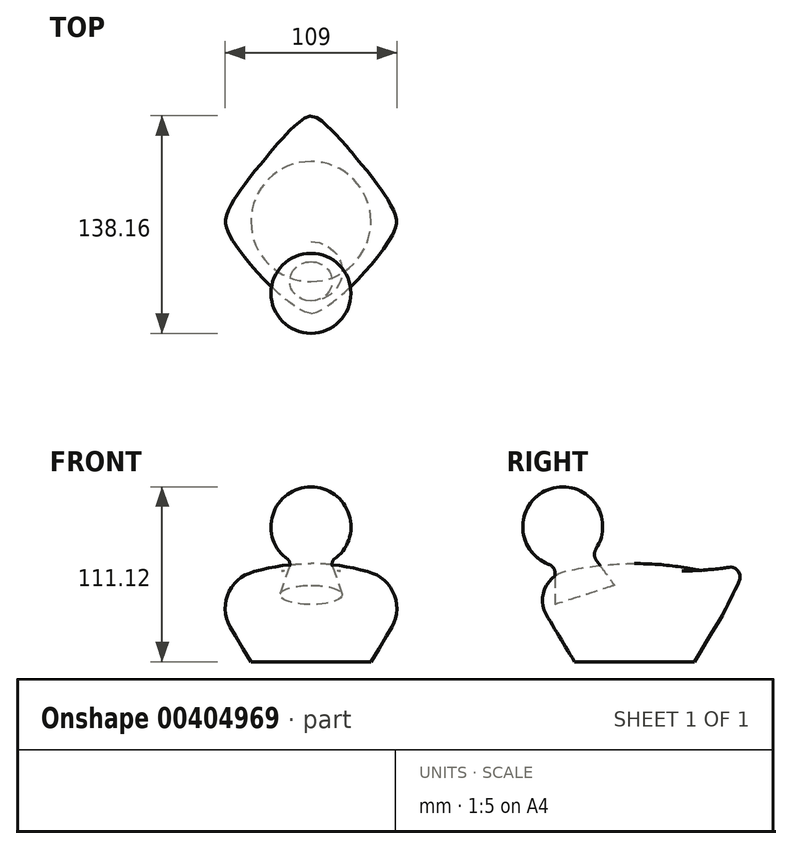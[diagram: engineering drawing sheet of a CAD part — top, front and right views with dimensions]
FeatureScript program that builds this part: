
annotation { "Feature Type Name" : "Feature", "Feature Type Description" : "" }
export const myFeature = defineFeature(function(context is Context, id is Id, definition is map)
    precondition{}
    {
        {
            var Q0;
            Q0=qCreatedBy(makeId("Top.planeOp"),FACE);
            var sketch = newSketch(context, id + "F0", { "sketchPlane" : qUnion([Q0])});
            skCircle(sketch, "E0", {"center": v(0, 0) * mm, "radius": 38.1 * mm});
            skSolve(sketch);
        }
        {
            var Q0;
            Q0=qCreatedBy(makeId("Right.planeOp"),FACE);
            var sketch = newSketch(context, id + "F1", { "sketchPlane" : qUnion([Q0])});
            skLineSegment(sketch, "E1.0", {"start": v(-38.1, 0) * mm, "end": v(38.1, 0) * mm, "construction": true});
            skLineSegment(sketch, "E2", {"start": v(-38.1, 0) * mm, "end": v(-55.66, 29.2) * mm});
            skLineSegment(sketch, "E3", {"start": v(38.1, 0) * mm, "end": v(55.66, 29.2) * mm});
            skLineSegment(sketch, "E4", {"start": v(-55.66, 29.2) * mm, "end": v(55.66, 29.2) * mm, "construction": true});
            skPoint(sketch, "E5.center.orphan", {"position": v(0, 29.2) * mm});
            skPoint(sketch, "E6.center.orphan", {"position": v(0, 968.99) * mm});
            skArc(sketch, "E7", {"start": v(43.4, 57.64) * mm, "mid": v(0, 62.33) * mm, "end": v(-43.4, 57.64) * mm});
            skArc(sketch, "E8", {"start": v(-43.4, 57.64) * mm, "mid": v(-56.83, 46.57) * mm, "end": v(-55.66, 29.2) * mm});
            skArc(sketch, "E9", {"start": v(55.66, 29.2) * mm, "mid": v(56.83, 46.57) * mm, "end": v(43.4, 57.64) * mm});
            skLineSegment(sketch, "E10", {"start": v(-39.34, 39.03) * mm, "end": v(39.34, 39.03) * mm, "construction": true});
            skSolve(sketch);
        }
        {
            var Q0;
            Q0=qCreatedBy(makeId("Front.planeOp"),FACE);
            var sketch = newSketch(context, id + "F2", { "sketchPlane" : qUnion([Q0])});
            skArc(sketch, "E11", {"start": v(37.58, 56.76) * mm, "mid": v(0, 62.33) * mm, "end": v(-37.58, 56.76) * mm});
            skLineSegment(sketch, "E12", {"start": v(-37.58, 56.76) * mm, "end": v(37.58, 56.76) * mm, "construction": true});
            skLineSegment(sketch, "E13", {"start": v(0, 56.76) * mm, "end": v(0, 62.33) * mm, "construction": true});
            skLineSegment(sketch, "E14.0", {"start": v(-38.1, 0) * mm, "end": v(38.1, 0) * mm, "construction": true});
            skLineSegment(sketch, "E15", {"start": v(-38.1, 0) * mm, "end": v(-51.1, 21.7) * mm, "construction": true});
            skPoint(sketch, "E16.start.orphan", {"position": v(-64.12, 43.4) * mm});
            skLineSegment(sketch, "E17", {"start": v(38.1, 0) * mm, "end": v(51.1, 21.7) * mm, "construction": true});
            skArc(sketch, "E18", {"start": v(-37.58, 56.76) * mm, "mid": v(-52.9, 42.53) * mm, "end": v(-51.1, 21.7) * mm});
            skArc(sketch, "E19", {"start": v(51.1, 21.7) * mm, "mid": v(52.9, 42.53) * mm, "end": v(37.58, 56.76) * mm});
            skLineSegment(sketch, "E20", {"start": v(-30.67, 33.95) * mm, "end": v(30.67, 33.95) * mm, "construction": true});
            skLineSegment(sketch, "E21.0", {"start": v(51.1, 21.7) * mm, "end": v(-51.1, 21.7) * mm, "construction": true});
            skSolve(sketch);
        }
        {
            var Q0;
            Q0=qCreatedBy(makeId("Right.planeOp"),FACE);
            var sketch = newSketch(context, id + "F3", { "sketchPlane" : qUnion([Q0])});
            skLineSegment(sketch, "E22.0", {"start": v(-38.1, 0) * mm, "end": v(-55.66, 29.2) * mm});
            skArc(sketch, "E23.0", {"start": v(-43.4, 57.64) * mm, "mid": v(-56.83, 46.57) * mm, "end": v(-55.66, 29.2) * mm});
            skArc(sketch, "E24.0", {"start": v(0, 62.33) * mm, "mid": v(-21.83, 61.15) * mm, "end": v(-43.4, 57.64) * mm});
            skPoint(sketch, "E25", {"position": v(0, 62.33) * mm});
            skPoint(sketch, "E26.orphan", {"position": v(43.4, 57.64) * mm});
            skSolve(sketch);
        }
        {
            var Q0;
            Q0=qCreatedBy(makeId("Front.planeOp"),FACE);
            var sketch = newSketch(context, id + "F4", { "sketchPlane" : qUnion([Q0])});
            skPoint(sketch, "E27.0", {"position": v(38.1, 0) * mm});
            skArc(sketch, "E28.0", {"start": v(51.1, 21.7) * mm, "mid": v(52.9, 42.53) * mm, "end": v(37.58, 56.76) * mm});
            skArc(sketch, "E29.0", {"start": v(37.58, 56.76) * mm, "mid": v(19, 60.93) * mm, "end": v(0, 62.33) * mm});
            skLineSegment(sketch, "E30.0", {"start": v(38.1, 0) * mm, "end": v(51.1, 21.7) * mm});
            skPoint(sketch, "E31.0", {"position": v(0, 62.33) * mm});
            skPoint(sketch, "E32.orphan", {"position": v(-37.58, 56.76) * mm});
            skSolve(sketch);
        }
        {
            var Q0;
            Q0=qCreatedBy(makeId("Right.planeOp"),FACE);
            var sketch = newSketch(context, id + "F5", { "sketchPlane" : qUnion([Q0])});
            skLineSegment(sketch, "E33.0", {"start": v(38.1, 0) * mm, "end": v(55.54, 29) * mm});
            skArc(sketch, "E34.0", {"start": v(42.31, 57.87) * mm, "mid": v(21.27, 61.21) * mm, "end": v(0, 62.33) * mm});
            skPoint(sketch, "E35.0", {"position": v(0, 62.33) * mm});
            skPoint(sketch, "E36.orphan", {"position": v(-43.4, 57.64) * mm});
            skPoint(sketch, "E37.0.end.orphan", {"position": v(43.4, 57.64) * mm});
            skPoint(sketch, "E37.0.start.orphan", {"position": v(55.66, 29.2) * mm});
            skPoint(sketch, "E38", {"position": v(71.96, 61.72) * mm});
            skLineSegment(sketch, "E39", {"start": v(55.77, 29.43) * mm, "end": v(66.52, 50.87) * mm});
            skLineSegment(sketch, "E40", {"start": v(44.53, 57.8) * mm, "end": v(59.94, 60) * mm});
            skArc(sketch, "E41.filletArc", {"start": v(42.31, 57.87) * mm, "mid": v(43.42, 57.74) * mm, "end": v(44.53, 57.8) * mm});
            skArc(sketch, "E42.filletArc", {"start": v(66.52, 50.87) * mm, "mid": v(66, 57.43) * mm, "end": v(59.94, 60) * mm});
            skArc(sketch, "E43.filletArc", {"start": v(55.54, 29) * mm, "mid": v(55.66, 29.21) * mm, "end": v(55.77, 29.43) * mm});
            skSolve(sketch);
        }
        {
            var Q0;
            Q0=qCreatedBy(makeId("Front.planeOp"),FACE);
            var sketch = newSketch(context, id + "F6", { "sketchPlane" : qUnion([Q0])});
            skLineSegment(sketch, "E44.0", {"start": v(-38.1, 0) * mm, "end": v(-51.1, 21.7) * mm});
            skArc(sketch, "E45.0", {"start": v(-37.58, 56.76) * mm, "mid": v(-52.9, 42.53) * mm, "end": v(-51.1, 21.7) * mm});
            skArc(sketch, "E46.0", {"start": v(0, 62.33) * mm, "mid": v(-19, 60.93) * mm, "end": v(-37.58, 56.76) * mm});
            skPoint(sketch, "E47.0", {"position": v(0, 62.33) * mm});
            skPoint(sketch, "E48.orphan", {"position": v(37.58, 56.76) * mm});
            skSolve(sketch);
        }
        {
            var Q0;
            Q0=sQuery(id+"F0.wireOp",EDGE,"E0");
            var Q1;
            Q1=sQuery(id+"F3.wireOp",VERTEX,"E25");
            var Q2;
            Q2 = qBodyType(qCreatedBy(id + "F4" ,EDGE), BodyType.WIRE);
            var Q3;
            Q3 = qBodyType(qCreatedBy(id + "F3" ,EDGE), BodyType.WIRE);
            var Q4;
            Q4 = qBodyType(qCreatedBy(id + "F5" ,EDGE), BodyType.WIRE);
            var Q5;
            Q5 = qBodyType(qCreatedBy(id + "F6" ,EDGE), BodyType.WIRE);
            loft(context, id + "F7", {"bodyType" : ToolBodyType.SURFACE, "addGuides" : true, "wireProfilesArray" : [{ "wireProfileEntities" : qUnion([Q0]) }, { "wireProfileEntities" : qUnion([Q1]) }], "guidesArray" : [{ "guideEntities" : qUnion([Q2]), "guideDerivativeType" : LoftGuideDerivativeType.DEFAULT, "guideDerivativeMagnitude" : 1 }, { "guideEntities" : qUnion([Q3]), "guideDerivativeType" : LoftGuideDerivativeType.DEFAULT, "guideDerivativeMagnitude" : 1 }, { "guideEntities" : qUnion([Q4]), "guideDerivativeType" : LoftGuideDerivativeType.DEFAULT, "guideDerivativeMagnitude" : 1 }, { "guideEntities" : qUnion([Q5]), "guideDerivativeType" : LoftGuideDerivativeType.DEFAULT, "guideDerivativeMagnitude" : 1 }]});
        }
        {
            var Q0;
            Q0=qCreatedBy(makeId("Right.planeOp"),FACE);
            var sketch = newSketch(context, id + "F8", { "sketchPlane" : qUnion([Q0])});
            skArc(sketch, "E49", {"start": v(-53.39, 109.88) * mm, "mid": v(-70.97, 86.32) * mm, "end": v(-54.52, 61.94) * mm});
            skLineSegment(sketch, "E50", {"start": v(-45.57, 85.72) * mm, "end": v(-31.6, 42.47) * mm, "construction": true});
            skLineSegment(sketch, "E51", {"start": v(-31.6, 42.47) * mm, "end": v(-50.4, 36.38) * mm, "construction": true});
            skLineSegment(sketch, "E52", {"start": v(-50.4, 36.38) * mm, "end": v(-50.4, 56) * mm});
            skLineSegment(sketch, "E53", {"start": v(-45.57, 85.72) * mm, "end": v(-53.39, 109.88) * mm, "construction": true});
            skPoint(sketch, "E54.visualSharp", {"position": v(-50.4, 60.78) * mm});
            skArc(sketch, "E54.filletArc", {"start": v(-50.4, 56) * mm, "mid": v(-51.54, 59.62) * mm, "end": v(-54.52, 61.94) * mm});
            skSolve(sketch);
        }
        {
            var Q0;
            Q0=sQuery(id+"F8.wireOp",EDGE,"E49");
            var Q1;
            Q1=sQuery(id+"F8.wireOp",EDGE,"E52");
            var Q2;
            Q2=sQuery(id+"F8.wireOp",EDGE,"E54.filletArc");
            var Q3;
            Q3=sQuery(id+"F8.wireOp",EDGE,"E50");
            revolve(context, id + "F9", {"bodyType" : ToolBodyType.SURFACE, "surfaceEntities" : qUnion([Q0, Q1, Q2]), "axis" : qUnion([Q3]), "revolveType" : RevolveType.FULL});
        }
        {
            var Q0;
            Q0=qCreatedBy(makeId("Right.planeOp"),FACE);
            var sketch = newSketch(context, id + "F10", { "sketchPlane" : qUnion([Q0])});
            skLineSegment(sketch, "E55", {"start": v(-62.17, 78.69) * mm, "end": v(-82.26, 64.78) * mm});
            skSolve(sketch);
        }
        {
            var Q0;
            Q0=sQuery(id+"F10.wireOp",EDGE,"E55");
            cPlane(context, id + "F11", {"entities" : qUnion([Q0]), "cplaneType" : CPlaneType.LINE_ANGLE, "offset" : 25.4 * mm, "angle" : 0 * degree, "width" : 152.4 * mm, "height" : 152.4 * mm});
        }
    });
